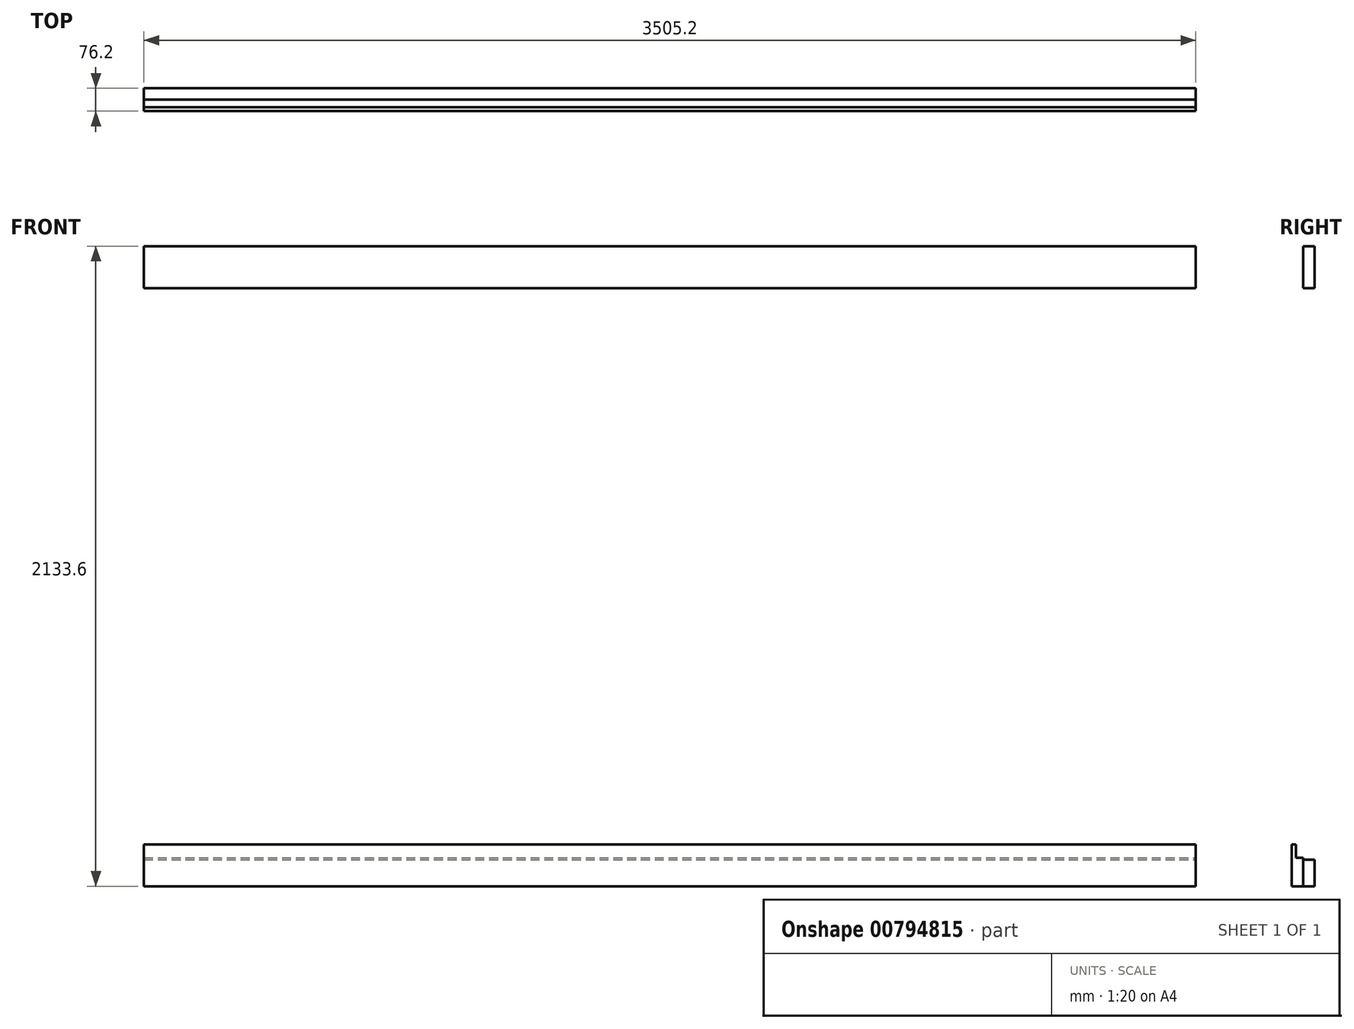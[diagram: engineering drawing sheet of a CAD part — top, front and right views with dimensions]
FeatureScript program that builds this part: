
annotation { "Feature Type Name" : "Feature", "Feature Type Description" : "" }
export const myFeature = defineFeature(function(context is Context, id is Id, definition is map)
    precondition{}
    {
        {
            var Q0;
            Q0=qCreatedBy(makeId("Front.planeOp"),FACE);
            var sketch = newSketch(context, id + "F0", { "sketchPlane" : qUnion([Q0])});
            skLineSegment(sketch, "E0.bottom", {"start": v(0, 0) * mm, "end": v(3505.2, 0) * mm});
            skLineSegment(sketch, "E0.top", {"start": v(0, -139.7) * mm, "end": v(3505.2, -139.7) * mm});
            skLineSegment(sketch, "E0.left", {"start": v(0, 0) * mm, "end": v(0, -139.7) * mm});
            skLineSegment(sketch, "E0.right", {"start": v(3505.2, 0) * mm, "end": v(3505.2, -139.7) * mm});
            skLineSegment(sketch, "E1.bottom", {"start": v(0, -2044.7) * mm, "end": v(3505.2, -2044.7) * mm});
            skLineSegment(sketch, "E1.top", {"start": v(0, -2133.6) * mm, "end": v(3505.2, -2133.6) * mm});
            skLineSegment(sketch, "E1.left", {"start": v(0, -2044.7) * mm, "end": v(0, -2133.6) * mm});
            skLineSegment(sketch, "E1.right", {"start": v(3505.2, -2044.7) * mm, "end": v(3505.2, -2133.6) * mm});
            skSolve(sketch);
        }
        {
            var Q0;
            Q0 = qSketchRegion(id + "F0", true);
            var Q1;
            Q1=makeQuery(id+"F0.imprint","IMPRINT",FACE,{"disambiguationData":[TD([[makeQuery(id+"F0.imprint","IMPRINT",EDGE,{"derivedFrom":sQuery(id+"F0.wireOp",EDGE,"6bd6dd3c-a4db-4971-9585-0563295c841c.1.0.0")}),-1.0]])]});
            var Q2;
            Q2=makeQuery(id+"F0.imprint","IMPRINT",FACE,{"disambiguationData":[TD([[makeQuery(id+"F0.imprint","IMPRINT",EDGE,{"derivedFrom":sQuery(id+"F0.wireOp",EDGE,"6bd6dd3c-a4db-4971-9585-0563295c841c.2.0.0")}),-1.0]])]});
            var Q3;
            Q3=makeQuery(id+"F0.imprint","IMPRINT",FACE,{"disambiguationData":[TD([[makeQuery(id+"F0.imprint","IMPRINT",EDGE,{"derivedFrom":sQuery(id+"F0.wireOp",EDGE,"SN2Asc0E-ntIz-6CfQ-WMqI-smQXnqOh4HoH.bottom")}),-1.0]])]});
            var Q4;
            Q4=makeQuery(id+"F0.imprint","IMPRINT",FACE,{"disambiguationData":[TD([[makeQuery(id+"F0.imprint","IMPRINT",EDGE,{"derivedFrom":sQuery(id+"F0.wireOp",EDGE,"YpWGKU8K-Umny-RZL1-ugtr-9FJp0mMLJ0gq.bottom")}),-1.0]])]});
            extrude(context, id + "F1", {"entities" : qUnion([Q0, Q1, Q2, Q3, Q4]), "depth" : 38.1 * mm, "offsetDistance" : 25.4 * mm});
        }
        {
            var Q0;
            Q0=makeQuery(id+"F1.opExtrude","SWEPT_FACE",FACE,{"disambiguationData":[OSD([sQuery(id+"F0.wireOp",EDGE,"E1.left")])]});
            var sketch = newSketch(context, id + "F2", { "sketchPlane" : qUnion([Q0])});
            skLineSegment(sketch, "E2.bottom", {"start": v(38.1, -2133.6) * mm, "end": v(76.2, -2133.6) * mm});
            skLineSegment(sketch, "E2.top", {"start": v(38.1, -1993.9) * mm, "end": v(76.2, -1993.9) * mm});
            skLineSegment(sketch, "E2.left", {"start": v(38.1, -2133.6) * mm, "end": v(38.1, -1993.9) * mm});
            skLineSegment(sketch, "E2.right", {"start": v(76.2, -2133.6) * mm, "end": v(76.2, -1993.9) * mm});
            skSolve(sketch);
        }
        {
            var Q0;
            Q0 = qSketchRegion(id + "F2", true);
            var Q1;
            Q1=makeQuery(id+"F1.opExtrude","SWEPT_FACE",FACE,{"disambiguationData":[OSD([sQuery(id+"F0.wireOp",EDGE,"E1.right")])]});
            extrude(context, id + "F3", {"entities" : qUnion([Q0]), "endBound" : BoundingType.UP_TO_SURFACE, "oppositeDirection" : true, "depth" : 25.4 * mm, "endBoundEntityFace" : qUnion([Q1]), "offsetDistance" : 25.4 * mm});
        }
        {
            var Q0;
            Q0=makeQuery(id+"F2.imprint","IMPRINT",FACE,{"disambiguationData":[TD([[makeQuery(id+"F2.imprint","IMPRINT",EDGE,{"derivedFrom":sQuery(id+"F2.wireOp",EDGE,"E2.left")}),-1.0]])]});
            var sketch = newSketch(context, id + "F4", { "sketchPlane" : qUnion([Q0])});
            skLineSegment(sketch, "E3.top", {"start": v(0, -2038.35) * mm, "end": v(62.6, -2038.35) * mm});
            skLineSegment(sketch, "E3.left", {"start": v(0, -1993.9) * mm, "end": v(0, -2038.35) * mm});
            skLineSegment(sketch, "E3.right", {"start": v(62.6, -1993.9) * mm, "end": v(62.6, -2038.35) * mm});
            skLineSegment(sketch, "E4", {"start": v(0, -1993.9) * mm, "end": v(62.6, -1993.9) * mm});
            skSolve(sketch);
        }
        {
            var Q0;
            Q0 = qSketchRegion(id + "F4", true);
            var Q1;
            Q1=makeQuery(id+"F1.opExtrude","SWEPT_FACE",FACE,{"disambiguationData":[OSD([sQuery(id+"F0.wireOp",EDGE,"E1.right")])]});
            extrude(context, id + "F5", {"entities" : qUnion([Q0]), "operationType" : NewBodyOperationType.REMOVE, "endBound" : BoundingType.UP_TO_SURFACE, "oppositeDirection" : true, "depth" : 25.4 * mm, "endBoundEntityFace" : qUnion([Q1]), "offsetDistance" : 25.4 * mm});
        }
    });
